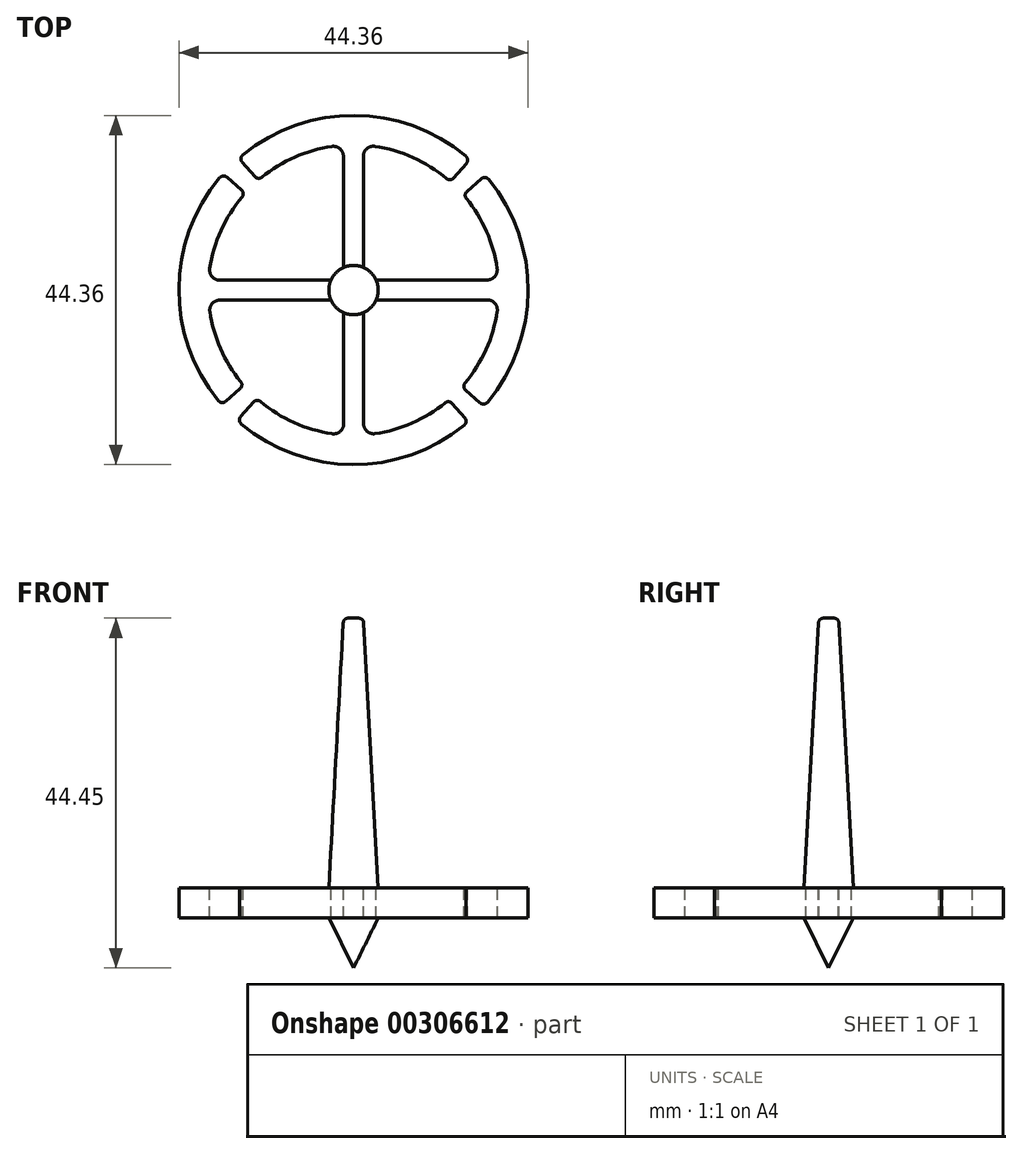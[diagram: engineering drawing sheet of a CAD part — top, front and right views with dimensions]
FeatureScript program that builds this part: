
annotation { "Feature Type Name" : "Feature", "Feature Type Description" : "" }
export const myFeature = defineFeature(function(context is Context, id is Id, definition is map)
    precondition{}
    {
        {
            var Q0;
            Q0=qCreatedBy(makeId("Front.planeOp"),FACE);
            var sketch = newSketch(context, id + "F0", { "sketchPlane" : qUnion([Q0])});
            skLineSegment(sketch, "E0", {"start": v(0, 0) * mm, "end": v(0, 44.45) * mm});
            skLineSegment(sketch, "E1", {"start": v(0, 44.45) * mm, "end": v(0.67, 44.45) * mm});
            skLineSegment(sketch, "E2", {"start": v(1.3, 43.85) * mm, "end": v(3.13, 10.16) * mm});
            skLineSegment(sketch, "E3.bottom", {"start": v(3.13, 10.16) * mm, "end": v(22.18, 10.16) * mm});
            skLineSegment(sketch, "E3.top", {"start": v(3.13, 6.35) * mm, "end": v(22.18, 6.35) * mm});
            skLineSegment(sketch, "E3.right", {"start": v(22.18, 10.16) * mm, "end": v(22.18, 6.35) * mm});
            skLineSegment(sketch, "E4", {"start": v(3.13, 6.35) * mm, "end": v(0, 0) * mm});
            skPoint(sketch, "E5.visualSharp", {"position": v(1.27, 44.45) * mm});
            skArc(sketch, "E5.filletArc", {"start": v(1.3, 43.85) * mm, "mid": v(1.1, 44.28) * mm, "end": v(0.67, 44.45) * mm});
            skSolve(sketch);
        }
        {
            var Q0;
            Q0 = qSketchRegion(id + "F0", true);
            var Q1;
            Q1=sQuery(id+"F0.wireOp",EDGE,"E0");
            revolve(context, id + "F1", {"entities" : qUnion([Q0]), "axis" : qUnion([Q1]), "revolveType" : RevolveType.FULL});
        }
        {
            var Q0;
            Q0=makeQuery(id+"F1.opRevolve","SWEPT_FACE",FACE,{"disambiguationData":[OSD([sQuery(id+"F0.wireOp",EDGE,"E3.bottom")])]});
            var sketch = newSketch(context, id + "F2", { "sketchPlane" : qUnion([Q0])});
            skArc(sketch, "E6", {"start": v(-2.75, 18.25) * mm, "mid": v(-7.45, 16.88) * mm, "end": v(-11.63, 14.32) * mm, "construction": true});
            skLineSegment(sketch, "E7.0", {"start": v(1.27, 2.86) * mm, "end": v(1.25, 17) * mm});
            skLineSegment(sketch, "E8.0", {"start": v(-1.27, 2.86) * mm, "end": v(-1.29, 17) * mm});
            skLineSegment(sketch, "E9", {"start": v(-12.5, 14.4) * mm, "end": v(-14.14, 16.24) * mm});
            skLineSegment(sketch, "E10.MirrorCS", {"start": v(12.72, 14.23) * mm, "end": v(14.33, 16.09) * mm});
            skArc(sketch, "E11", {"start": v(14.26, 16.99) * mm, "mid": v(0.13, 22.18) * mm, "end": v(-14.07, 17.15) * mm});
            skPoint(sketch, "E12.end.orphan", {"position": v(0, 18.45) * mm});
            skPoint(sketch, "E12.start.orphan", {"position": v(0, 5.08) * mm});
            skArc(sketch, "E13.trimOffspring", {"start": v(11.84, 14.16) * mm, "mid": v(7.55, 16.84) * mm, "end": v(2.7, 18.25) * mm, "construction": true});
            skPoint(sketch, "E14.visualSharp", {"position": v(-12.1, 13.93) * mm});
            skArc(sketch, "E14.filletArc", {"start": v(-12.5, 14.4) * mm, "mid": v(-12.09, 14.18) * mm, "end": v(-11.63, 14.32) * mm});
            skPoint(sketch, "E15.visualSharp", {"position": v(-14.57, 16.72) * mm});
            skArc(sketch, "E15.filletArc", {"start": v(-14.07, 17.15) * mm, "mid": v(-14.3, 16.7) * mm, "end": v(-14.14, 16.24) * mm});
            skPoint(sketch, "E16.visualSharp", {"position": v(14.75, 16.57) * mm});
            skArc(sketch, "E16.filletArc", {"start": v(14.33, 16.09) * mm, "mid": v(14.49, 16.55) * mm, "end": v(14.26, 16.99) * mm});
            skPoint(sketch, "E17.visualSharp", {"position": v(12.3, 13.75) * mm});
            skArc(sketch, "E17.filletArc", {"start": v(11.84, 14.16) * mm, "mid": v(12.3, 14.01) * mm, "end": v(12.72, 14.23) * mm});
            skPoint(sketch, "E18.visualSharp", {"position": v(-1.29, 18.4) * mm});
            skArc(sketch, "E18.filletArc", {"start": v(-1.29, 17) * mm, "mid": v(-1.73, 17.96) * mm, "end": v(-2.75, 18.25) * mm});
            skPoint(sketch, "E19.visualSharp", {"position": v(1.25, 18.41) * mm});
            skArc(sketch, "E19.filletArc", {"start": v(2.7, 18.25) * mm, "mid": v(1.7, 17.96) * mm, "end": v(1.25, 17) * mm});
            skLineSegment(sketch, "E20.1.0", {"start": v(-14.4, -12.5) * mm, "end": v(-16.24, -14.14) * mm});
            skPoint(sketch, "E20.1.1", {"position": v(-18.41, 1.25) * mm});
            skPoint(sketch, "E20.1.2", {"position": v(-16.57, 14.75) * mm});
            skPoint(sketch, "E20.1.3", {"position": v(-13.75, 12.3) * mm});
            skPoint(sketch, "E20.1.4", {"position": v(-18.4, -1.29) * mm});
            skLineSegment(sketch, "E20.1.5", {"start": v(-2.86, -1.27) * mm, "end": v(-17, -1.29) * mm});
            skArc(sketch, "E20.1.6", {"start": v(-17, -1.29) * mm, "mid": v(-17.96, -1.73) * mm, "end": v(-18.25, -2.75) * mm});
            skPoint(sketch, "E20.1.7", {"position": v(-18.45, 0) * mm});
            skArc(sketch, "E20.1.8", {"start": v(-18.25, 2.7) * mm, "mid": v(-17.96, 1.7) * mm, "end": v(-17, 1.25) * mm});
            skPoint(sketch, "E20.1.9", {"position": v(-16.72, -14.57) * mm});
            skPoint(sketch, "E20.1.10", {"position": v(-13.93, -12.1) * mm});
            skArc(sketch, "E20.1.11", {"start": v(-18.25, -2.75) * mm, "mid": v(-16.88, -7.45) * mm, "end": v(-14.32, -11.63) * mm});
            skLineSegment(sketch, "E20.1.12", {"start": v(-2.86, 1.27) * mm, "end": v(-17, 1.25) * mm});
            skArc(sketch, "E20.1.13", {"start": v(-14.16, 11.84) * mm, "mid": v(-16.84, 7.55) * mm, "end": v(-18.25, 2.7) * mm, "construction": true});
            skLineSegment(sketch, "E20.1.14", {"start": v(-14.23, 12.72) * mm, "end": v(-16.09, 14.33) * mm});
            skArc(sketch, "E20.1.16", {"start": v(-17.15, -14.07) * mm, "mid": v(-16.7, -14.3) * mm, "end": v(-16.24, -14.14) * mm});
            skArc(sketch, "E20.1.17", {"start": v(-14.16, 11.84) * mm, "mid": v(-14.01, 12.3) * mm, "end": v(-14.23, 12.72) * mm});
            skArc(sketch, "E20.1.18", {"start": v(-16.09, 14.33) * mm, "mid": v(-16.55, 14.49) * mm, "end": v(-16.99, 14.26) * mm});
            skArc(sketch, "E20.1.19", {"start": v(-14.4, -12.5) * mm, "mid": v(-14.18, -12.09) * mm, "end": v(-14.32, -11.63) * mm});
            skLineSegment(sketch, "E20.2.0", {"start": v(12.5, -14.4) * mm, "end": v(14.14, -16.24) * mm});
            skPoint(sketch, "E20.2.1", {"position": v(-1.25, -18.41) * mm});
            skPoint(sketch, "E20.2.2", {"position": v(-14.75, -16.57) * mm});
            skPoint(sketch, "E20.2.3", {"position": v(-12.3, -13.75) * mm});
            skPoint(sketch, "E20.2.4", {"position": v(1.29, -18.4) * mm});
            skLineSegment(sketch, "E20.2.5", {"start": v(1.27, -2.86) * mm, "end": v(1.29, -17) * mm});
            skArc(sketch, "E20.2.6", {"start": v(1.29, -17) * mm, "mid": v(1.73, -17.96) * mm, "end": v(2.75, -18.25) * mm});
            skPoint(sketch, "E20.2.7", {"position": v(0, -18.45) * mm});
            skArc(sketch, "E20.2.8", {"start": v(-2.7, -18.25) * mm, "mid": v(-1.7, -17.96) * mm, "end": v(-1.25, -17) * mm});
            skPoint(sketch, "E20.2.9", {"position": v(14.57, -16.72) * mm});
            skPoint(sketch, "E20.2.10", {"position": v(12.1, -13.93) * mm});
            skArc(sketch, "E20.2.11", {"start": v(2.75, -18.25) * mm, "mid": v(7.45, -16.88) * mm, "end": v(11.63, -14.32) * mm, "construction": true});
            skLineSegment(sketch, "E20.2.12", {"start": v(-1.27, -2.86) * mm, "end": v(-1.25, -17) * mm});
            skArc(sketch, "E20.2.13", {"start": v(-11.84, -14.16) * mm, "mid": v(-7.55, -16.84) * mm, "end": v(-2.7, -18.25) * mm, "construction": true});
            skLineSegment(sketch, "E20.2.14", {"start": v(-12.72, -14.23) * mm, "end": v(-14.33, -16.09) * mm});
            skArc(sketch, "E20.2.16", {"start": v(14.07, -17.15) * mm, "mid": v(14.3, -16.7) * mm, "end": v(14.14, -16.24) * mm});
            skArc(sketch, "E20.2.17", {"start": v(-11.84, -14.16) * mm, "mid": v(-12.3, -14.01) * mm, "end": v(-12.72, -14.23) * mm});
            skArc(sketch, "E20.2.18", {"start": v(-14.33, -16.09) * mm, "mid": v(-14.49, -16.55) * mm, "end": v(-14.26, -16.99) * mm});
            skArc(sketch, "E20.2.19", {"start": v(12.5, -14.4) * mm, "mid": v(12.09, -14.18) * mm, "end": v(11.63, -14.32) * mm});
            skLineSegment(sketch, "E20.3.0", {"start": v(14.4, 12.5) * mm, "end": v(16.24, 14.14) * mm});
            skPoint(sketch, "E20.3.1", {"position": v(18.41, -1.25) * mm});
            skPoint(sketch, "E20.3.2", {"position": v(16.57, -14.75) * mm});
            skPoint(sketch, "E20.3.3", {"position": v(13.75, -12.3) * mm});
            skPoint(sketch, "E20.3.4", {"position": v(18.4, 1.29) * mm});
            skLineSegment(sketch, "E20.3.5", {"start": v(2.86, 1.27) * mm, "end": v(17, 1.29) * mm});
            skArc(sketch, "E20.3.6", {"start": v(17, 1.29) * mm, "mid": v(17.96, 1.73) * mm, "end": v(18.25, 2.75) * mm});
            skPoint(sketch, "E20.3.7", {"position": v(18.45, 0) * mm});
            skArc(sketch, "E20.3.8", {"start": v(18.25, -2.7) * mm, "mid": v(17.96, -1.7) * mm, "end": v(17, -1.25) * mm});
            skPoint(sketch, "E20.3.9", {"position": v(16.72, 14.57) * mm});
            skPoint(sketch, "E20.3.10", {"position": v(13.93, 12.1) * mm});
            skArc(sketch, "E20.3.11", {"start": v(18.25, 2.75) * mm, "mid": v(16.88, 7.45) * mm, "end": v(14.32, 11.63) * mm, "construction": true});
            skLineSegment(sketch, "E20.3.12", {"start": v(2.86, -1.27) * mm, "end": v(17, -1.25) * mm});
            skArc(sketch, "E20.3.13", {"start": v(14.16, -11.84) * mm, "mid": v(16.84, -7.55) * mm, "end": v(18.25, -2.7) * mm, "construction": true});
            skLineSegment(sketch, "E20.3.14", {"start": v(14.23, -12.72) * mm, "end": v(16.09, -14.33) * mm});
            skArc(sketch, "E20.3.16", {"start": v(17.15, 14.07) * mm, "mid": v(16.7, 14.3) * mm, "end": v(16.24, 14.14) * mm});
            skArc(sketch, "E20.3.17", {"start": v(14.16, -11.84) * mm, "mid": v(14.01, -12.3) * mm, "end": v(14.23, -12.72) * mm});
            skArc(sketch, "E20.3.18", {"start": v(16.09, -14.33) * mm, "mid": v(16.55, -14.49) * mm, "end": v(16.99, -14.26) * mm});
            skArc(sketch, "E20.3.19", {"start": v(14.4, 12.5) * mm, "mid": v(14.18, 12.09) * mm, "end": v(14.32, 11.63) * mm});
            skArc(sketch, "E21.trimOffspring", {"start": v(-14.16, 11.84) * mm, "mid": v(-16.84, 7.55) * mm, "end": v(-18.25, 2.7) * mm});
            skArc(sketch, "E22.trimOffspring", {"start": v(-2.75, 18.25) * mm, "mid": v(-7.45, 16.88) * mm, "end": v(-11.63, 14.32) * mm});
            skArc(sketch, "E23.trimOffspring", {"start": v(11.84, 14.16) * mm, "mid": v(7.55, 16.84) * mm, "end": v(2.7, 18.25) * mm});
            skArc(sketch, "E24.trimOffspring", {"start": v(18.25, 2.75) * mm, "mid": v(16.88, 7.45) * mm, "end": v(14.32, 11.63) * mm});
            skArc(sketch, "E25.trimOffspring", {"start": v(14.16, -11.84) * mm, "mid": v(16.84, -7.55) * mm, "end": v(18.25, -2.7) * mm});
            skArc(sketch, "E26.trimOffspring", {"start": v(2.75, -18.25) * mm, "mid": v(7.45, -16.88) * mm, "end": v(11.63, -14.32) * mm});
            skArc(sketch, "E27.trimOffspring", {"start": v(-11.84, -14.16) * mm, "mid": v(-7.55, -16.84) * mm, "end": v(-2.7, -18.25) * mm});
            skArc(sketch, "E28", {"start": v(-17.15, -14.07) * mm, "mid": v(-15.77, -15.6) * mm, "end": v(-14.26, -16.99) * mm});
            skArc(sketch, "E29.trimOffspring", {"start": v(14.07, -17.15) * mm, "mid": v(15.6, -15.77) * mm, "end": v(16.99, -14.26) * mm});
            skArc(sketch, "E30.trimOffspring", {"start": v(17.15, 14.07) * mm, "mid": v(0.13, 22.18) * mm, "end": v(-16.99, 14.26) * mm});
            skLineSegment(sketch, "E31", {"start": v(-17, -1.29) * mm, "end": v(-2.86, -1.27) * mm});
            skArc(sketch, "E32", {"start": v(-2.86, -1.27) * mm, "mid": v(-2.22, -2.21) * mm, "end": v(-1.27, -2.86) * mm});
            skArc(sketch, "E33.trimOffspring", {"start": v(-1.27, 2.86) * mm, "mid": v(-2.21, 2.22) * mm, "end": v(-2.86, 1.27) * mm});
            skArc(sketch, "E34.trimOffspring", {"start": v(2.86, 1.27) * mm, "mid": v(2.22, 2.21) * mm, "end": v(1.27, 2.86) * mm});
            skArc(sketch, "E35.trimOffspring", {"start": v(1.27, -2.86) * mm, "mid": v(2.21, -2.22) * mm, "end": v(2.86, -1.27) * mm});
            skSolve(sketch);
        }
        {
            var Q0;
            Q0 = qSketchRegion(id + "F2", true);
            extrude(context, id + "F3", {"entities" : qUnion([Q0]), "operationType" : NewBodyOperationType.REMOVE, "oppositeDirection" : true, "depth" : 25.4 * mm});
        }
    });
